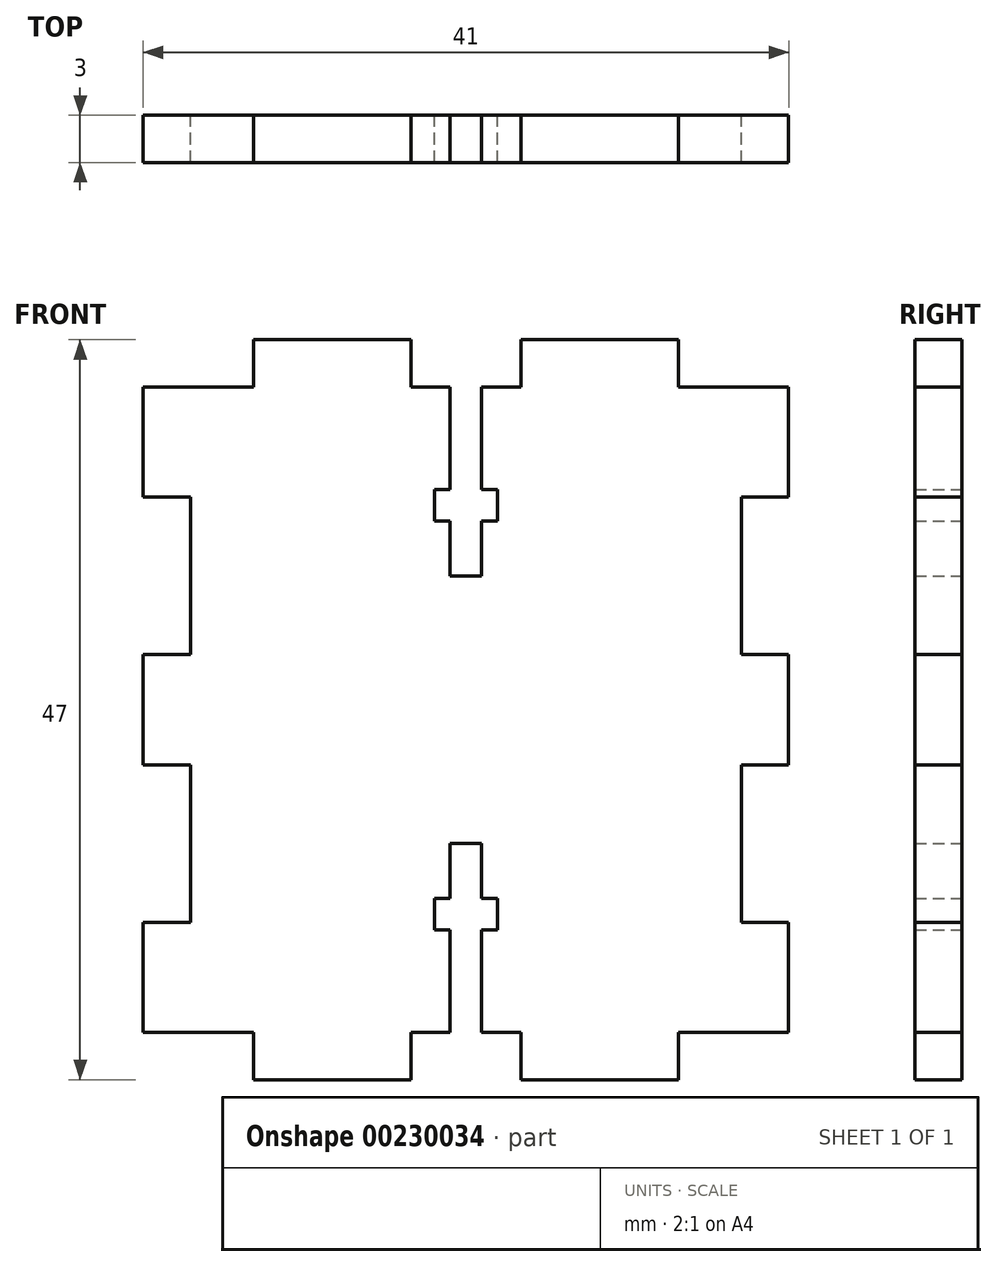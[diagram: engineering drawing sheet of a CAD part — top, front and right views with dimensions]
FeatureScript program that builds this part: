
annotation { "Feature Type Name" : "Feature", "Feature Type Description" : "" }
export const myFeature = defineFeature(function(context is Context, id is Id, definition is map)
    precondition{}
    {
        {
            var Q0;
            Q0=qCreatedBy(makeId("Front.planeOp"),FACE);
            var sketch = newSketch(context, id + "F0", { "sketchPlane" : qUnion([Q0])});
            skLineSegment(sketch, "E0", {"start": v(-48.37, 17.06) * mm, "end": v(-48.37, 20.56) * mm});
            skLineSegment(sketch, "E1", {"start": v(-48.37, 20.56) * mm, "end": v(-47.37, 20.56) * mm});
            skLineSegment(sketch, "E2", {"start": v(-47.37, 20.56) * mm, "end": v(-47.37, 22.56) * mm});
            skLineSegment(sketch, "E3", {"start": v(-47.37, 22.56) * mm, "end": v(-48.37, 22.56) * mm});
            skLineSegment(sketch, "E4", {"start": v(-48.37, 22.56) * mm, "end": v(-48.37, 29.06) * mm});
            skLineSegment(sketch, "E5", {"start": v(-48.37, 29.06) * mm, "end": v(-45.87, 29.06) * mm});
            skLineSegment(sketch, "E6", {"start": v(-45.87, 29.06) * mm, "end": v(-45.87, 32.06) * mm});
            skLineSegment(sketch, "E7", {"start": v(-45.87, 32.06) * mm, "end": v(-35.87, 32.06) * mm});
            skLineSegment(sketch, "E8", {"start": v(-35.87, 32.06) * mm, "end": v(-35.87, 29.06) * mm});
            skLineSegment(sketch, "E9", {"start": v(-35.87, 29.06) * mm, "end": v(-28.87, 29.06) * mm});
            skPoint(sketch, "E10.end.orphan", {"position": v(-52.03, 29.06) * mm});
            skPoint(sketch, "E11.start.orphan", {"position": v(-49.53, 29.06) * mm});
            skLineSegment(sketch, "E12", {"start": v(-48.37, 17.06) * mm, "end": v(-49.37, 17.06) * mm});
            skLineSegment(sketch, "E13", {"start": v(-28.87, 29.06) * mm, "end": v(-28.87, 22.06) * mm});
            skLineSegment(sketch, "E14", {"start": v(-28.87, 22.06) * mm, "end": v(-31.87, 22.06) * mm});
            skLineSegment(sketch, "E15", {"start": v(-31.87, 22.06) * mm, "end": v(-31.87, 12.06) * mm});
            skLineSegment(sketch, "E16", {"start": v(-31.87, 12.06) * mm, "end": v(-28.87, 12.06) * mm});
            skLineSegment(sketch, "E17", {"start": v(-28.87, 12.06) * mm, "end": v(-28.87, 8.56) * mm});
            skLineSegment(sketch, "E18", {"start": v(-45.87, 32.06) * mm, "end": v(-49.37, 32.06) * mm, "construction": true});
            skLineSegment(sketch, "E19", {"start": v(-49.37, 32.06) * mm, "end": v(-49.37, 8.56) * mm, "construction": true});
            skLineSegment(sketch, "E20.MirrorCS", {"start": v(-50.37, 20.56) * mm, "end": v(-51.37, 20.56) * mm});
            skLineSegment(sketch, "E21.MirrorCS", {"start": v(-66.87, 12.06) * mm, "end": v(-69.87, 12.06) * mm});
            skLineSegment(sketch, "E22.MirrorCS", {"start": v(-51.37, 20.56) * mm, "end": v(-51.37, 22.56) * mm});
            skLineSegment(sketch, "E23.MirrorCS", {"start": v(-51.37, 22.56) * mm, "end": v(-50.37, 22.56) * mm});
            skLineSegment(sketch, "E24.MirrorCS", {"start": v(-50.37, 17.06) * mm, "end": v(-49.37, 17.06) * mm});
            skLineSegment(sketch, "E25.MirrorCS", {"start": v(-69.87, 22.06) * mm, "end": v(-66.87, 22.06) * mm});
            skLineSegment(sketch, "E26.MirrorCS", {"start": v(-52.87, 29.06) * mm, "end": v(-52.87, 32.06) * mm});
            skLineSegment(sketch, "E27.MirrorCS", {"start": v(-62.87, 32.06) * mm, "end": v(-62.87, 29.06) * mm});
            skLineSegment(sketch, "E28.MirrorCS", {"start": v(-50.37, 29.06) * mm, "end": v(-52.87, 29.06) * mm});
            skLineSegment(sketch, "E29.MirrorCS", {"start": v(-50.37, 17.06) * mm, "end": v(-50.37, 20.56) * mm});
            skLineSegment(sketch, "E30.MirrorCS", {"start": v(-52.87, 32.06) * mm, "end": v(-49.37, 32.06) * mm, "construction": true});
            skLineSegment(sketch, "E31.MirrorCS", {"start": v(-50.37, 22.56) * mm, "end": v(-50.37, 29.06) * mm});
            skPoint(sketch, "E32.MirrorP", {"position": v(-49.21, 29.06) * mm});
            skLineSegment(sketch, "E33.MirrorCS", {"start": v(-69.87, 29.06) * mm, "end": v(-69.87, 22.06) * mm});
            skLineSegment(sketch, "E34.MirrorCS", {"start": v(-69.87, 12.06) * mm, "end": v(-69.87, 8.56) * mm});
            skLineSegment(sketch, "E35.MirrorCS", {"start": v(-62.87, 29.06) * mm, "end": v(-69.87, 29.06) * mm});
            skLineSegment(sketch, "E36.MirrorCS", {"start": v(-66.87, 22.06) * mm, "end": v(-66.87, 12.06) * mm});
            skLineSegment(sketch, "E37.MirrorCS", {"start": v(-52.87, 32.06) * mm, "end": v(-62.87, 32.06) * mm});
            skPoint(sketch, "E38.MirrorP", {"position": v(-46.71, 29.06) * mm});
            skLineSegment(sketch, "E39", {"start": v(-69.87, 8.56) * mm, "end": v(-28.87, 8.56) * mm, "construction": true});
            skLineSegment(sketch, "E40.MirrorCS", {"start": v(-48.37, -3.44) * mm, "end": v(-47.37, -3.44) * mm});
            skLineSegment(sketch, "E41.MirrorCS", {"start": v(-47.37, -3.44) * mm, "end": v(-47.37, -5.44) * mm});
            skLineSegment(sketch, "E42.MirrorCS", {"start": v(-52.87, -14.94) * mm, "end": v(-49.37, -14.94) * mm, "construction": true});
            skLineSegment(sketch, "E43.MirrorCS", {"start": v(-51.37, -5.44) * mm, "end": v(-50.37, -5.44) * mm});
            skLineSegment(sketch, "E44.MirrorCS", {"start": v(-48.37, 0.06) * mm, "end": v(-48.37, -3.44) * mm});
            skLineSegment(sketch, "E45.MirrorCS", {"start": v(-45.87, -14.94) * mm, "end": v(-49.37, -14.94) * mm, "construction": true});
            skLineSegment(sketch, "E46.MirrorCS", {"start": v(-50.37, -3.44) * mm, "end": v(-51.37, -3.44) * mm});
            skLineSegment(sketch, "E47.MirrorCS", {"start": v(-51.37, -3.44) * mm, "end": v(-51.37, -5.44) * mm});
            skLineSegment(sketch, "E48.MirrorCS", {"start": v(-50.37, 0.06) * mm, "end": v(-49.37, 0.06) * mm});
            skLineSegment(sketch, "E49.MirrorCS", {"start": v(-48.37, 0.06) * mm, "end": v(-49.37, 0.06) * mm});
            skLineSegment(sketch, "E50.MirrorCS", {"start": v(-50.37, 0.06) * mm, "end": v(-50.37, -3.44) * mm});
            skLineSegment(sketch, "E51.MirrorCS", {"start": v(-50.37, -11.94) * mm, "end": v(-52.87, -11.94) * mm});
            skLineSegment(sketch, "E52.MirrorCS", {"start": v(-52.87, -11.94) * mm, "end": v(-52.87, -14.94) * mm});
            skLineSegment(sketch, "E53.MirrorCS", {"start": v(-66.87, 5.06) * mm, "end": v(-69.87, 5.06) * mm});
            skLineSegment(sketch, "E54.MirrorCS", {"start": v(-31.87, 5.06) * mm, "end": v(-28.87, 5.06) * mm});
            skLineSegment(sketch, "E55.MirrorCS", {"start": v(-28.87, 5.06) * mm, "end": v(-28.87, 8.56) * mm});
            skLineSegment(sketch, "E56.MirrorCS", {"start": v(-45.87, -11.94) * mm, "end": v(-45.87, -14.94) * mm});
            skLineSegment(sketch, "E57.MirrorCS", {"start": v(-47.37, -5.44) * mm, "end": v(-48.37, -5.44) * mm});
            skLineSegment(sketch, "E58.MirrorCS", {"start": v(-35.87, -14.94) * mm, "end": v(-35.87, -11.94) * mm});
            skLineSegment(sketch, "E59.MirrorCS", {"start": v(-69.87, -4.94) * mm, "end": v(-66.87, -4.94) * mm});
            skLineSegment(sketch, "E60.MirrorCS", {"start": v(-62.87, -14.94) * mm, "end": v(-62.87, -11.94) * mm});
            skLineSegment(sketch, "E61.MirrorCS", {"start": v(-28.87, -4.94) * mm, "end": v(-31.87, -4.94) * mm});
            skLineSegment(sketch, "E62.MirrorCS", {"start": v(-69.87, 5.06) * mm, "end": v(-69.87, 8.56) * mm});
            skLineSegment(sketch, "E63.MirrorCS", {"start": v(-48.37, -11.94) * mm, "end": v(-45.87, -11.94) * mm});
            skPoint(sketch, "E64.MirrorP", {"position": v(-49.21, -11.94) * mm});
            skLineSegment(sketch, "E65.MirrorCS", {"start": v(-48.37, -5.44) * mm, "end": v(-48.37, -11.94) * mm});
            skLineSegment(sketch, "E66.MirrorCS", {"start": v(-50.37, -5.44) * mm, "end": v(-50.37, -11.94) * mm});
            skLineSegment(sketch, "E67.MirrorCS", {"start": v(-62.87, -11.94) * mm, "end": v(-69.87, -11.94) * mm});
            skLineSegment(sketch, "E68.MirrorCS", {"start": v(-69.87, -11.94) * mm, "end": v(-69.87, -4.94) * mm});
            skLineSegment(sketch, "E69.MirrorCS", {"start": v(-49.37, -14.94) * mm, "end": v(-49.37, 8.56) * mm, "construction": true});
            skLineSegment(sketch, "E70.MirrorCS", {"start": v(-31.87, -4.94) * mm, "end": v(-31.87, 5.06) * mm});
            skPoint(sketch, "E71.MirrorP", {"position": v(-52.03, -11.94) * mm});
            skLineSegment(sketch, "E72.MirrorCS", {"start": v(-66.87, -4.94) * mm, "end": v(-66.87, 5.06) * mm});
            skLineSegment(sketch, "E73.MirrorCS", {"start": v(-45.87, -14.94) * mm, "end": v(-35.87, -14.94) * mm});
            skPoint(sketch, "E74.MirrorP", {"position": v(-49.53, -11.94) * mm});
            skLineSegment(sketch, "E75.MirrorCS", {"start": v(-35.87, -11.94) * mm, "end": v(-28.87, -11.94) * mm});
            skPoint(sketch, "E76.MirrorP", {"position": v(-46.71, -11.94) * mm});
            skLineSegment(sketch, "E77.MirrorCS", {"start": v(-52.87, -14.94) * mm, "end": v(-62.87, -14.94) * mm});
            skLineSegment(sketch, "E78.MirrorCS", {"start": v(-28.87, -11.94) * mm, "end": v(-28.87, -4.94) * mm});
            skSolve(sketch);
        }
        {
            var Q0;
            Q0 = qSketchRegion(id + "F0", true);
            extrude(context, id + "F1", {"entities" : qUnion([Q0]), "depth" : 3 * mm});
        }
    });
